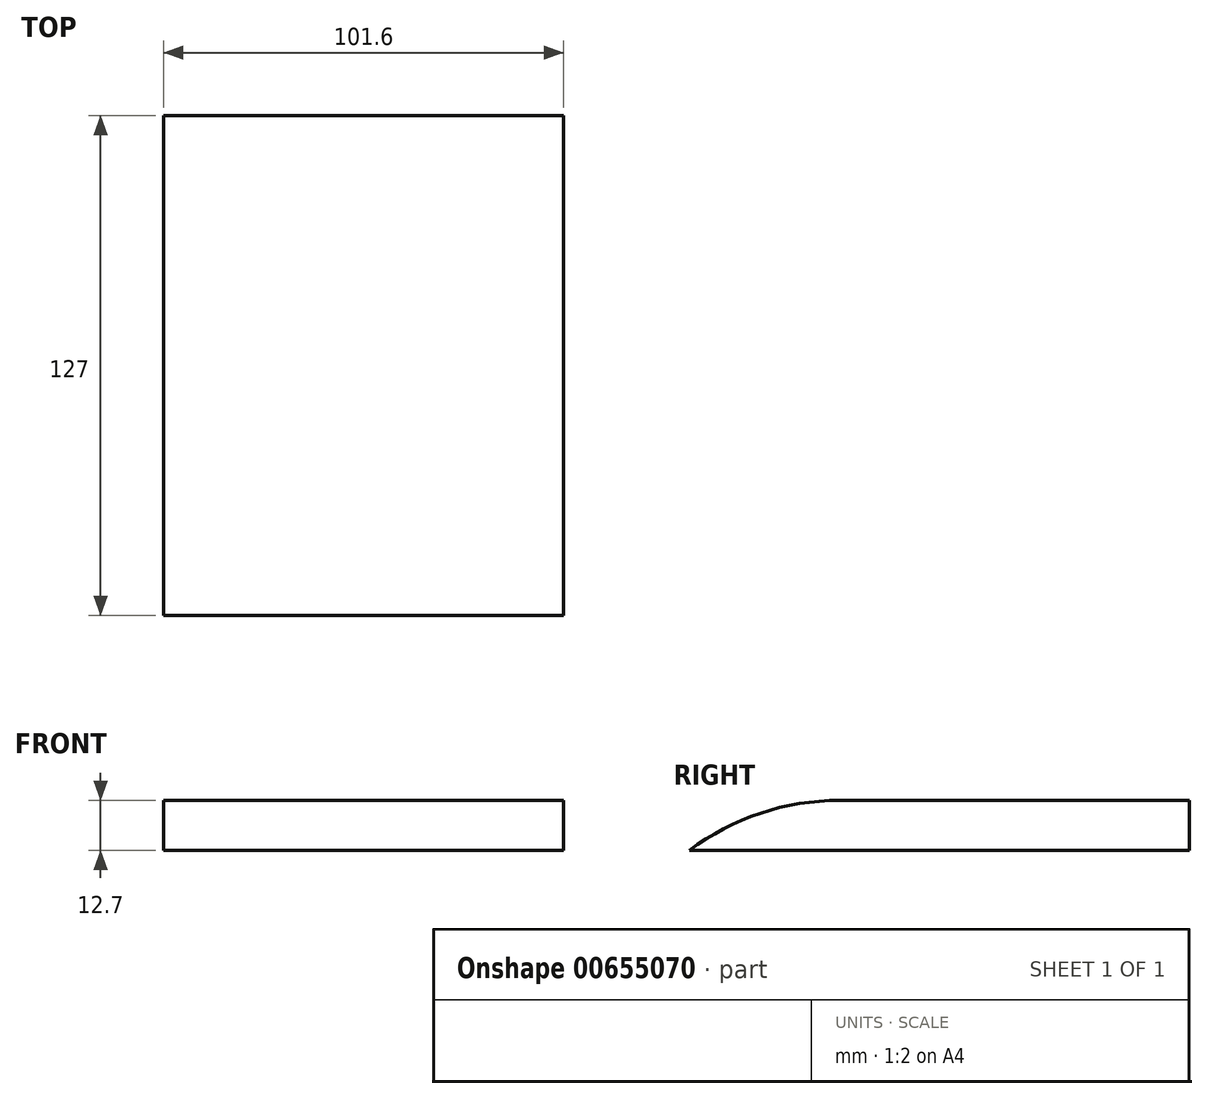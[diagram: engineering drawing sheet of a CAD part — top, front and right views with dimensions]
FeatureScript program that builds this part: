
annotation { "Feature Type Name" : "Feature", "Feature Type Description" : "" }
export const myFeature = defineFeature(function(context is Context, id is Id, definition is map)
    precondition{}
    {
        {
            var Q0;
            Q0=qCreatedBy(makeId("Front.planeOp"),FACE);
            var sketch = newSketch(context, id + "F0", { "sketchPlane" : qUnion([Q0])});
            skLineSegment(sketch, "E0.bottom", {"start": v(50.8, -6.35) * mm, "end": v(-50.8, -6.35) * mm});
            skLineSegment(sketch, "E0.top", {"start": v(50.8, 6.35) * mm, "end": v(-50.8, 6.35) * mm});
            skLineSegment(sketch, "E0.left", {"start": v(50.8, -6.35) * mm, "end": v(50.8, 6.35) * mm});
            skLineSegment(sketch, "E0.right", {"start": v(-50.8, -6.35) * mm, "end": v(-50.8, 6.35) * mm});
            skPoint(sketch, "E0.middle", {"position": v(0, 0) * mm});
            skSolve(sketch);
        }
        {
            var Q0;
            Q0=makeQuery(id+"F0.imprint","IMPRINT",FACE,{"disambiguationData":[TD([[makeQuery(id+"F0.imprint","IMPRINT",EDGE,{"derivedFrom":sQuery(id+"F0.wireOp",EDGE,"E0.bottom")}),-1.0]])]});
            extrude(context, id + "F1", {"entities" : qUnion([Q0]), "depth" : 63.5 * mm, "offsetDistance" : 25.4 * mm, "hasSecondDirection" : true, "secondDirectionOppositeDirection" : true, "secondDirectionDepth" : 63.5 * mm});
        }
        {
            var Q0;
            Q0=makeQuery(id+"F1.opExtrude","CAP_EDGE",EDGE,{"disambiguationData":[OSD([sQuery(id+"F0.wireOp",EDGE,"E0.top")])],"isStart":false});
            fillet(context, id + "F2", {"entities" : qUnion([Q0]), "radius" : 63.5 * mm, "tangentPropagation" : true, "allowEdgeOverflow" : false});
        }
    });
